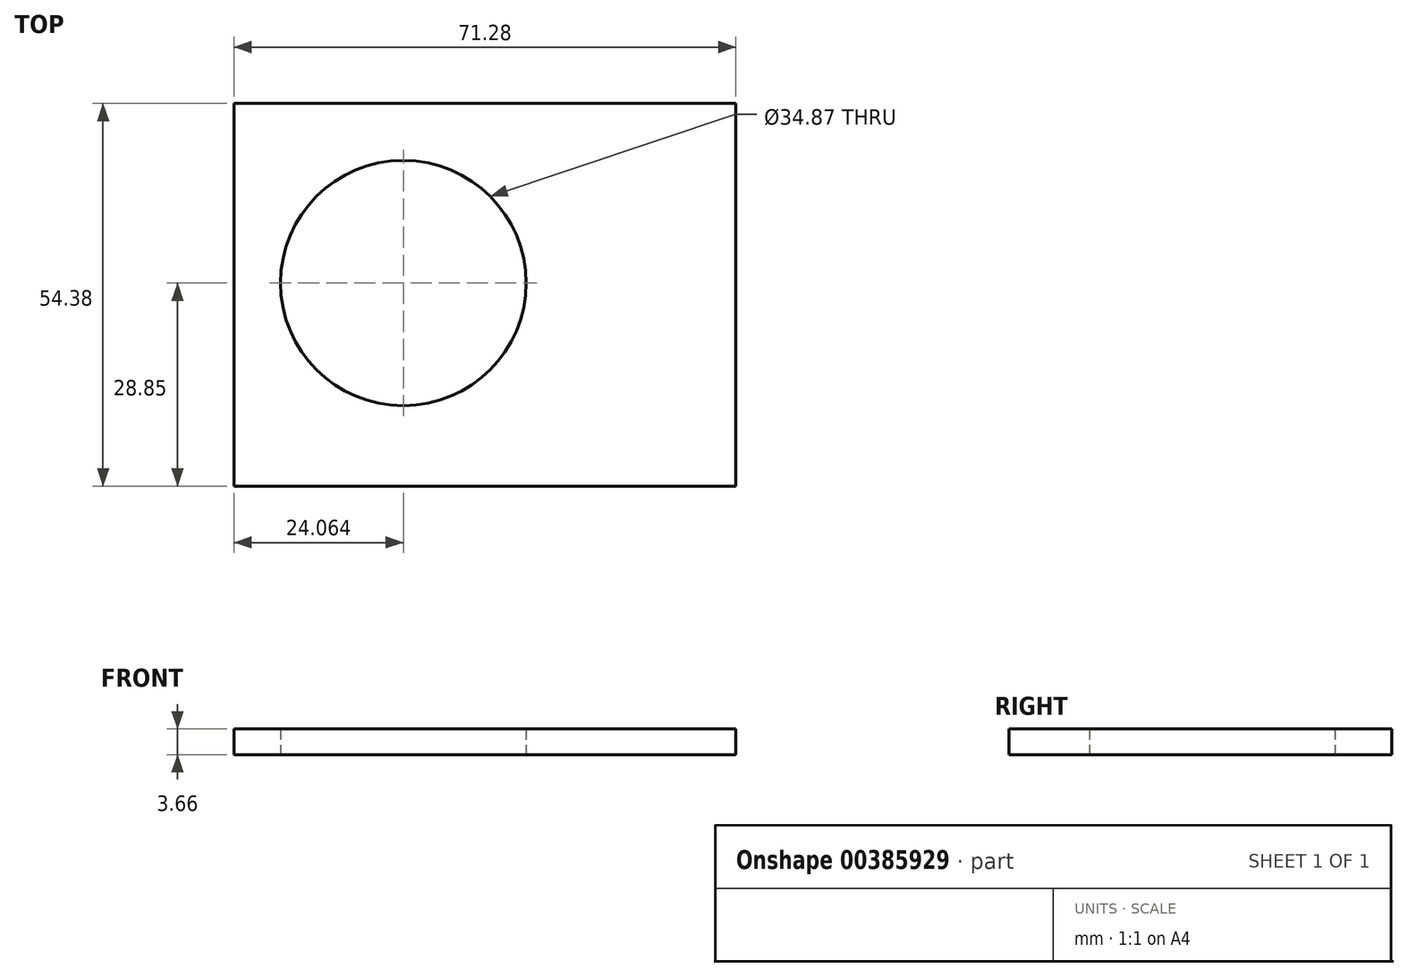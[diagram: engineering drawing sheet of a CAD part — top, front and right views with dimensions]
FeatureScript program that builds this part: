
annotation { "Feature Type Name" : "Feature", "Feature Type Description" : "" }
export const myFeature = defineFeature(function(context is Context, id is Id, definition is map)
    precondition{}
    {
        {
            var Q0;
            Q0=qCreatedBy(makeId("Top.planeOp"),FACE);
            var sketch = newSketch(context, id + "F0", { "sketchPlane" : qUnion([Q0])});
            skLineSegment(sketch, "E0.bottom", {"start": v(-40.41, 25.53) * mm, "end": v(30.87, 25.53) * mm});
            skLineSegment(sketch, "E0.top", {"start": v(-40.41, -28.85) * mm, "end": v(30.87, -28.85) * mm});
            skLineSegment(sketch, "E0.left", {"start": v(-40.41, 25.53) * mm, "end": v(-40.41, -28.85) * mm});
            skLineSegment(sketch, "E0.right", {"start": v(30.87, 25.53) * mm, "end": v(30.87, -28.85) * mm});
            skCircle(sketch, "E1", {"center": v(-16.35, 0) * mm, "radius": 17.44 * mm});
            skSolve(sketch);
        }
        {
            var Q0;
            Q0=makeQuery(id+"F0.imprint","IMPRINT",FACE,{"disambiguationData":[TD([[makeQuery(id+"F0.imprint","IMPRINT",EDGE,{"derivedFrom":sQuery(id+"F0.wireOp",EDGE,"E0.bottom")}),-1.0]])]});
            extrude(context, id + "F1", {"entities" : qUnion([Q0]), "depth" : 3.66 * mm});
        }
    });
